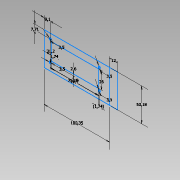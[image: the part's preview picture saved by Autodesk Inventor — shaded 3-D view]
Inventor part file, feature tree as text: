
AUTODESK INVENTOR PART (.ipt)
format: ipt  version: 2015 SP1 (Build 190203100, 203)  size: 78,848 bytes
history: native  units: mm
features: sketch x1
ambient origin geometry x8: Origin, YZ Plane, XZ Plane, XY Plane, X Axis, Y Axis, Z Axis, Center Point
feature tree (1):
  sketch  "Sketch1"  dims[d0=100.35mm d1=50.18mm d2=3.5mm d3=3.5mm d4=3.5mm d5=3.5mm d6=75.18mm d7=31.2mm d8=7.71mm d9=9.1mm d10=12.0mm d11=71.7mm d12=26.0mm d13=2.6mm d14=1.74mm d15=1.74mm]
